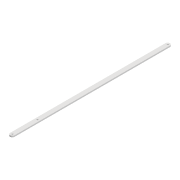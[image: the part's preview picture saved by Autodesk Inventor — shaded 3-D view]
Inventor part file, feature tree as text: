
AUTODESK INVENTOR PART (.ipt)
format: ipt  version: 2022 (Build 260153000, 153)  size: 92,672 bytes
history: native  units: mm
features: extrude x1, sketch x1
ambient origin geometry x8: Origin, YZ Plane, XZ Plane, XY Plane, X Axis, Y Axis, Z Axis, Center Point
bodies: Solid1 (feature_tree)
feature tree (2):
  extrude  "Extrusion1"  Depth=57.376mm
  sketch  "Sketch1"  dims[d0=3.3mm d1=3.3mm d2=10.0mm d3=355.998mm d6=3.0mm d7=0.0mm d14=3.3mm d15=57.376mm]
